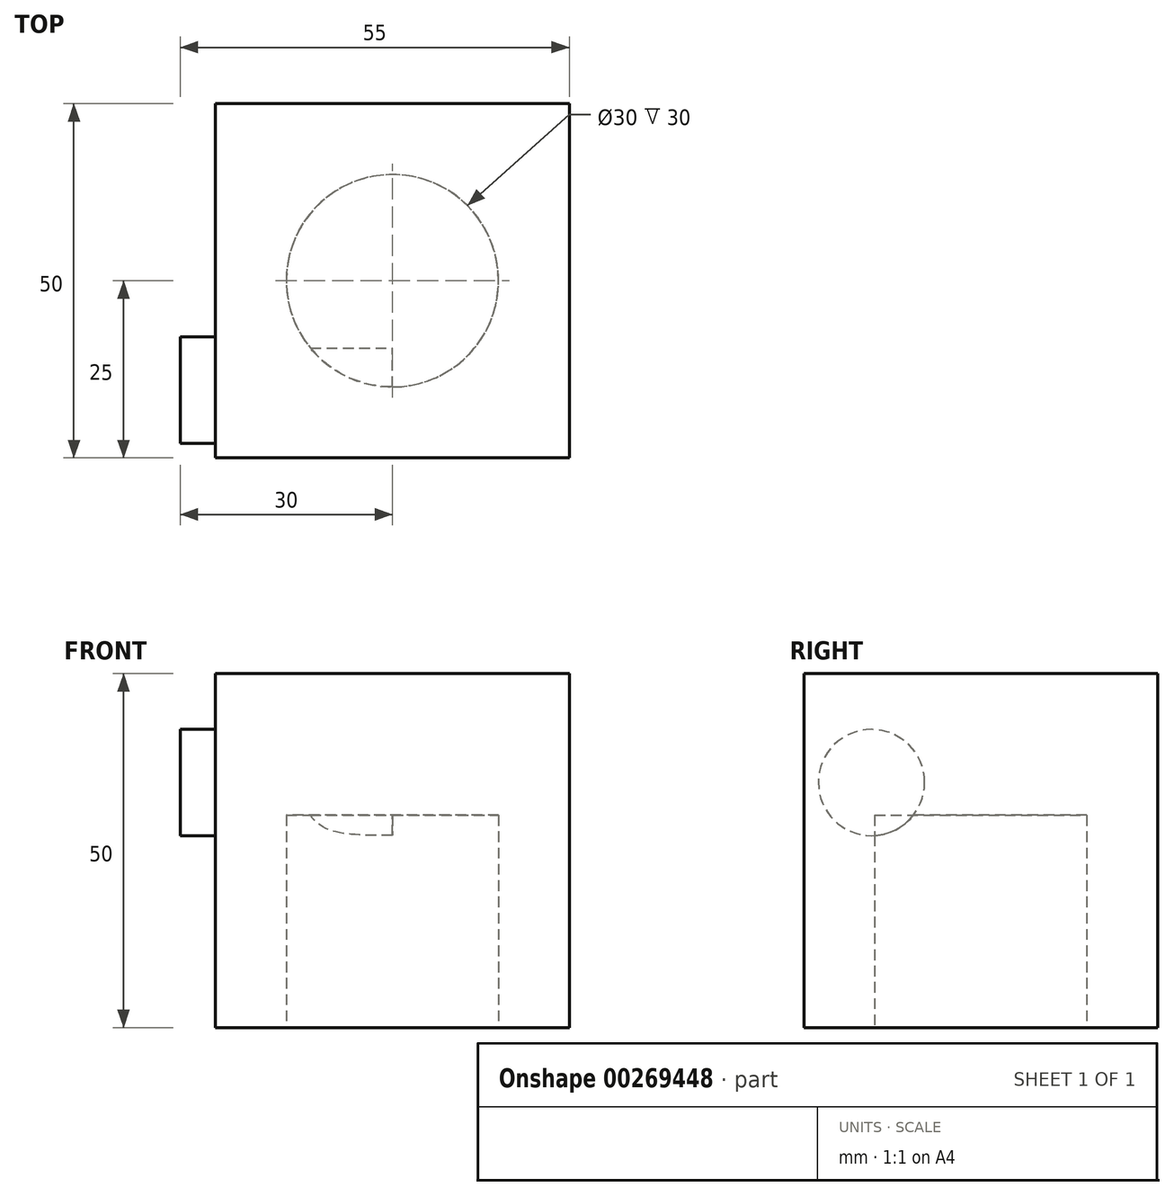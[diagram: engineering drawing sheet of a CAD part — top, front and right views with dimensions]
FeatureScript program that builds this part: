
annotation { "Feature Type Name" : "Feature", "Feature Type Description" : "" }
export const myFeature = defineFeature(function(context is Context, id is Id, definition is map)
    precondition{}
    {
        {
            var Q0;
            Q0=qCreatedBy(makeId("Top.planeOp"),FACE);
            var sketch = newSketch(context, id + "F0", { "sketchPlane" : qUnion([Q0])});
            skLineSegment(sketch, "E0.bottom", {"start": v(-25, 25) * mm, "end": v(25, 25) * mm});
            skLineSegment(sketch, "E0.top", {"start": v(-25, -25) * mm, "end": v(25, -25) * mm});
            skLineSegment(sketch, "E0.left", {"start": v(-25, 25) * mm, "end": v(-25, -25) * mm});
            skLineSegment(sketch, "E0.right", {"start": v(25, 25) * mm, "end": v(25, -25) * mm});
            skPoint(sketch, "E0.middle", {"position": v(0, 0) * mm});
            skSolve(sketch);
        }
        {
            var Q0;
            Q0 = qSketchRegion(id + "F0", true);
            extrude(context, id + "F1", {"entities" : qUnion([Q0]), "depth" : 50 * mm});
        }
        {
            var Q0;
            Q0=qCreatedBy(makeId("Top.planeOp"),FACE);
            var sketch = newSketch(context, id + "F2", { "sketchPlane" : qUnion([Q0])});
            skCircle(sketch, "E1", {"center": v(0, 0) * mm, "radius": 15 * mm});
            skSolve(sketch);
        }
        {
            var Q0;
            Q0 = qSketchRegion(id + "F2", true);
            extrude(context, id + "F3", {"entities" : qUnion([Q0]), "operationType" : NewBodyOperationType.REMOVE, "depth" : 30 * mm});
        }
        {
            var Q0;
            Q0=qCreatedBy(makeId("Right.planeOp"),FACE);
            var sketch = newSketch(context, id + "F4", { "sketchPlane" : qUnion([Q0])});
            skCircle(sketch, "E2", {"center": v(-15.45, 34.62) * mm, "radius": 7.5 * mm});
            skSolve(sketch);
        }
        {
            var Q0;
            Q0 = qSketchRegion(id + "F4", true);
            extrude(context, id + "F5", {"entities" : qUnion([Q0]), "operationType" : NewBodyOperationType.ADD, "oppositeDirection" : true, "depth" : 30 * mm});
        }
    });
